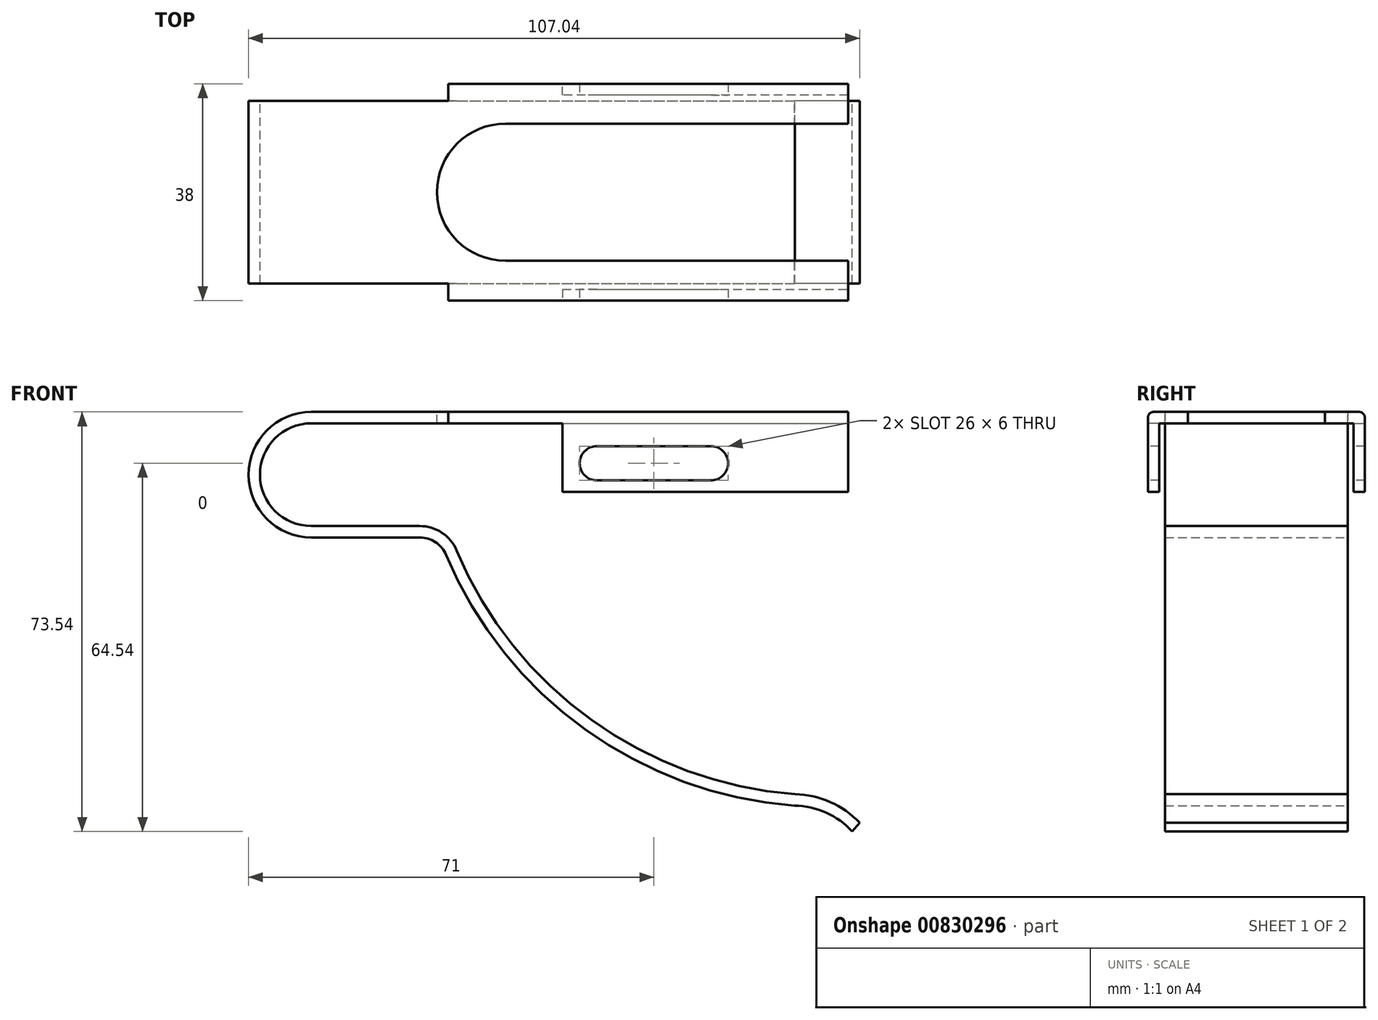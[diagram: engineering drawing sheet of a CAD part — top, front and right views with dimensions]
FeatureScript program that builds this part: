
annotation { "Feature Type Name" : "Feature", "Feature Type Description" : "" }
export const myFeature = defineFeature(function(context is Context, id is Id, definition is map)
    precondition{}
    {
        {
            var Q0;
            Q0=qCreatedBy(makeId("Front.planeOp"),FACE);
            var sketch = newSketch(context, id + "F0", { "sketchPlane" : qUnion([Q0])});
            skArc(sketch, "E0", {"start": v(0, 11) * mm, "mid": v(-11, 0) * mm, "end": v(0, -11) * mm});
            skLineSegment(sketch, "E1", {"start": v(0, 11) * mm, "end": v(94, 11) * mm});
            skLineSegment(sketch, "E2", {"start": v(0, -11) * mm, "end": v(19, -11) * mm});
            skArc(sketch, "E3", {"start": v(23.61, -14.06) * mm, "mid": v(47.92, -44.63) * mm, "end": v(84.61, -58) * mm});
            skPoint(sketch, "E4.visualSharp", {"position": v(22.4, -11) * mm});
            skArc(sketch, "E4.filletArc", {"start": v(23.61, -14.06) * mm, "mid": v(21.77, -11.84) * mm, "end": v(19, -11) * mm});
            skArc(sketch, "E5", {"start": v(94.75, -62.54) * mm, "mid": v(90.15, -59.22) * mm, "end": v(84.61, -58) * mm});
            skLineSegment(sketch, "E6.0", {"start": v(0, 9) * mm, "end": v(94, 9) * mm});
            skArc(sketch, "E6.1", {"start": v(0, 9) * mm, "mid": v(-9, 0) * mm, "end": v(0, -9) * mm});
            skArc(sketch, "E6.2", {"start": v(96.04, -61) * mm, "mid": v(90.88, -57.36) * mm, "end": v(84.7, -56) * mm});
            skArc(sketch, "E6.3", {"start": v(25.45, -13.3) * mm, "mid": v(49.07, -42.99) * mm, "end": v(84.7, -56) * mm});
            skArc(sketch, "E6.4", {"start": v(25.45, -13.3) * mm, "mid": v(22.88, -10.17) * mm, "end": v(19, -9) * mm});
            skLineSegment(sketch, "E6.5", {"start": v(0, -9) * mm, "end": v(19, -9) * mm});
            skLineSegment(sketch, "E7", {"start": v(94, 11) * mm, "end": v(94, 9) * mm});
            skLineSegment(sketch, "E8", {"start": v(96.04, -61) * mm, "end": v(94.75, -62.54) * mm});
            skLineSegment(sketch, "E9", {"start": v(96.04, -61) * mm, "end": v(104.04, -61) * mm, "construction": true});
            skSolve(sketch);
        }
        {
            var Q0;
            Q0=qSketchRegion(id+"F0",true);
            extrude(context, id + "F1", {"entities" : qUnion([Q0]), "depth" : 16 * mm, "offsetDistance" : 25 * mm});
        }
        {
            var Q0;
            Q0=makeQuery(id+"F1.opExtrude","SWEPT_FACE",FACE,{"disambiguationData":[OSD([sQuery(id+"F0.wireOp",EDGE,"E1")])]});
            var sketch = newSketch(context, id + "F2", { "sketchPlane" : qUnion([Q0])});
            skLineSegment(sketch, "E10.bottom", {"start": v(94, -16) * mm, "end": v(24, -16) * mm});
            skLineSegment(sketch, "E10.top", {"start": v(94, -19) * mm, "end": v(24, -19) * mm});
            skLineSegment(sketch, "E10.left", {"start": v(94, -16) * mm, "end": v(94, -19) * mm});
            skLineSegment(sketch, "E10.right", {"start": v(24, -16) * mm, "end": v(24, -19) * mm});
            skSolve(sketch);
        }
        {
            var Q0;
            Q0=qSketchRegion(id+"F2",true);
            extrude(context, id + "F3", {"entities" : qUnion([Q0]), "operationType" : NewBodyOperationType.ADD, "oppositeDirection" : true, "depth" : 2 * mm, "offsetDistance" : 25 * mm});
        }
        {
            var Q0;
            Q0=makeQuery(id+"F3.opExtrude","SWEPT_FACE",FACE,{"disambiguationData":[OSD([sQuery(id+"F2.wireOp",EDGE,"E10.top")])]});
            var sketch = newSketch(context, id + "F4", { "sketchPlane" : qUnion([Q0])});
            skLineSegment(sketch, "E11.bottom", {"start": v(94, 11) * mm, "end": v(44, 11) * mm});
            skLineSegment(sketch, "E11.top", {"start": v(94, -3) * mm, "end": v(44, -3) * mm});
            skLineSegment(sketch, "E11.left", {"start": v(94, 11) * mm, "end": v(94, -3) * mm});
            skLineSegment(sketch, "E11.right", {"start": v(44, 11) * mm, "end": v(44, -3) * mm});
            skSolve(sketch);
        }
        {
            var Q0;
            Q0=qSketchRegion(id+"F4",true);
            extrude(context, id + "F5", {"entities" : qUnion([Q0]), "operationType" : NewBodyOperationType.ADD, "oppositeDirection" : true, "depth" : 2 * mm, "offsetDistance" : 25 * mm});
        }
        {
            var Q0;
            Q0=makeQuery(id+"F3.opExtrude","CAP_EDGE",EDGE,{"disambiguationData":[OSD([sQuery(id+"F2.wireOp",EDGE,"E10.top")])],"isStart":true});
            fillet(context, id + "F6", {"entities" : qUnion([Q0]), "radius" : 1 * mm, "allowEdgeOverflow" : false});
        }
        {
            var Q0;
            Q0=makeQuery(id+"F1.opExtrude","SWEPT_BODY",BODY,{"disambiguationData":[OSD([sQuery(id+"F0.wireOp",EDGE,"E0"),sQuery(id+"F0.wireOp",EDGE,"E1"),sQuery(id+"F0.wireOp",EDGE,"E2"),sQuery(id+"F0.wireOp",EDGE,"E3"),sQuery(id+"F0.wireOp",EDGE,"E4.filletArc"),sQuery(id+"F0.wireOp",EDGE,"E5"),sQuery(id+"F0.wireOp",EDGE,"E6.0"),sQuery(id+"F0.wireOp",EDGE,"E6.1"),sQuery(id+"F0.wireOp",EDGE,"E6.2"),sQuery(id+"F0.wireOp",EDGE,"E6.3"),sQuery(id+"F0.wireOp",EDGE,"E6.4"),sQuery(id+"F0.wireOp",EDGE,"E6.5"),sQuery(id+"F0.wireOp",EDGE,"E7"),sQuery(id+"F0.wireOp",EDGE,"E8")])]});
            var Q1;
            Q1=qCreatedBy(makeId("Front.planeOp"),FACE);
            mirror(context, id + "F7", {"operationType" : NewBodyOperationType.ADD, "entities" : qUnion([Q0]), "mirrorPlane" : qUnion([Q1])});
        }
        {
            var Q0;
            {var subQ0=makeQuery(id+"F3.boolean.opBoolean","MERGE",FACE,{"derivedFrom":[makeQuery(id+"F1.opExtrude","SWEPT_FACE",FACE,{"disambiguationData":[OSD([sQuery(id+"F0.wireOp",EDGE,"E1")])]}),makeQuery(id+"F3.opExtrude","CAP_FACE",FACE,{"disambiguationData":[OSD([sQuery(id+"F2.wireOp",EDGE,"E10.bottom"),sQuery(id+"F2.wireOp",EDGE,"E10.top"),sQuery(id+"F2.wireOp",EDGE,"E10.left"),sQuery(id+"F2.wireOp",EDGE,"E10.right")])],"isStart":true})]});Q0=makeQuery(id+"F7.boolean.opBoolean","MERGE",FACE,{"derivedFrom":[subQ0,makeQuery(id+"F7.opPattern","COPY",FACE,{"derivedFrom":subQ0,"instanceName":"1"})]});}
            var sketch = newSketch(context, id + "F8", { "sketchPlane" : qUnion([Q0])});
            skArc(sketch, "E12", {"start": v(34, 12) * mm, "mid": v(22, 0) * mm, "end": v(34, -12) * mm});
            skLineSegment(sketch, "E13", {"start": v(34, 12) * mm, "end": v(94, 12) * mm});
            skLineSegment(sketch, "E14", {"start": v(34, -12) * mm, "end": v(94, -12) * mm});
            skLineSegment(sketch, "E15", {"start": v(94, 12) * mm, "end": v(94, -12) * mm});
            skSolve(sketch);
        }
        {
            var Q0;
            Q0=qSketchRegion(id+"F8",true);
            extrude(context, id + "F9", {"entities" : qUnion([Q0]), "operationType" : NewBodyOperationType.REMOVE, "oppositeDirection" : true, "depth" : 2 * mm, "offsetDistance" : 25 * mm});
        }
        {
            var Q0;
            Q0=makeQuery(id+"F5.boolean.opBoolean","MERGE",FACE,{"derivedFrom":[makeQuery(id+"F3.opExtrude","SWEPT_FACE",FACE,{"disambiguationData":[OSD([sQuery(id+"F2.wireOp",EDGE,"E10.top")])]}),makeQuery(id+"F5.opExtrude","CAP_FACE",FACE,{"disambiguationData":[OSD([sQuery(id+"F4.wireOp",EDGE,"E11.bottom"),sQuery(id+"F4.wireOp",EDGE,"E11.top"),sQuery(id+"F4.wireOp",EDGE,"E11.left"),sQuery(id+"F4.wireOp",EDGE,"E11.right")])],"isStart":true})]});
            var sketch = newSketch(context, id + "F10", { "sketchPlane" : qUnion([Q0])});
            skLineSegment(sketch, "E16", {"start": v(50, 2) * mm, "end": v(70, 2) * mm});
            skArc(sketch, "E17.0.startCap", {"start": v(50, -1) * mm, "mid": v(47, 2) * mm, "end": v(50, 5) * mm});
            skArc(sketch, "E17.0.endCap", {"start": v(70, 5) * mm, "mid": v(73, 2) * mm, "end": v(70, -1) * mm});
            skLineSegment(sketch, "E17.0.left", {"start": v(50, 5) * mm, "end": v(70, 5) * mm});
            skLineSegment(sketch, "E17.0.right", {"start": v(50, -1) * mm, "end": v(70, -1) * mm});
            skSolve(sketch);
        }
        {
            var Q0;
            Q0=qSketchRegion(id+"F10",true);
            extrude(context, id + "F11", {"entities" : qUnion([Q0]), "operationType" : NewBodyOperationType.REMOVE, "endBound" : BoundingType.THROUGH_ALL, "oppositeDirection" : true, "depth" : 25 * mm, "offsetDistance" : 25 * mm});
        }
    });
